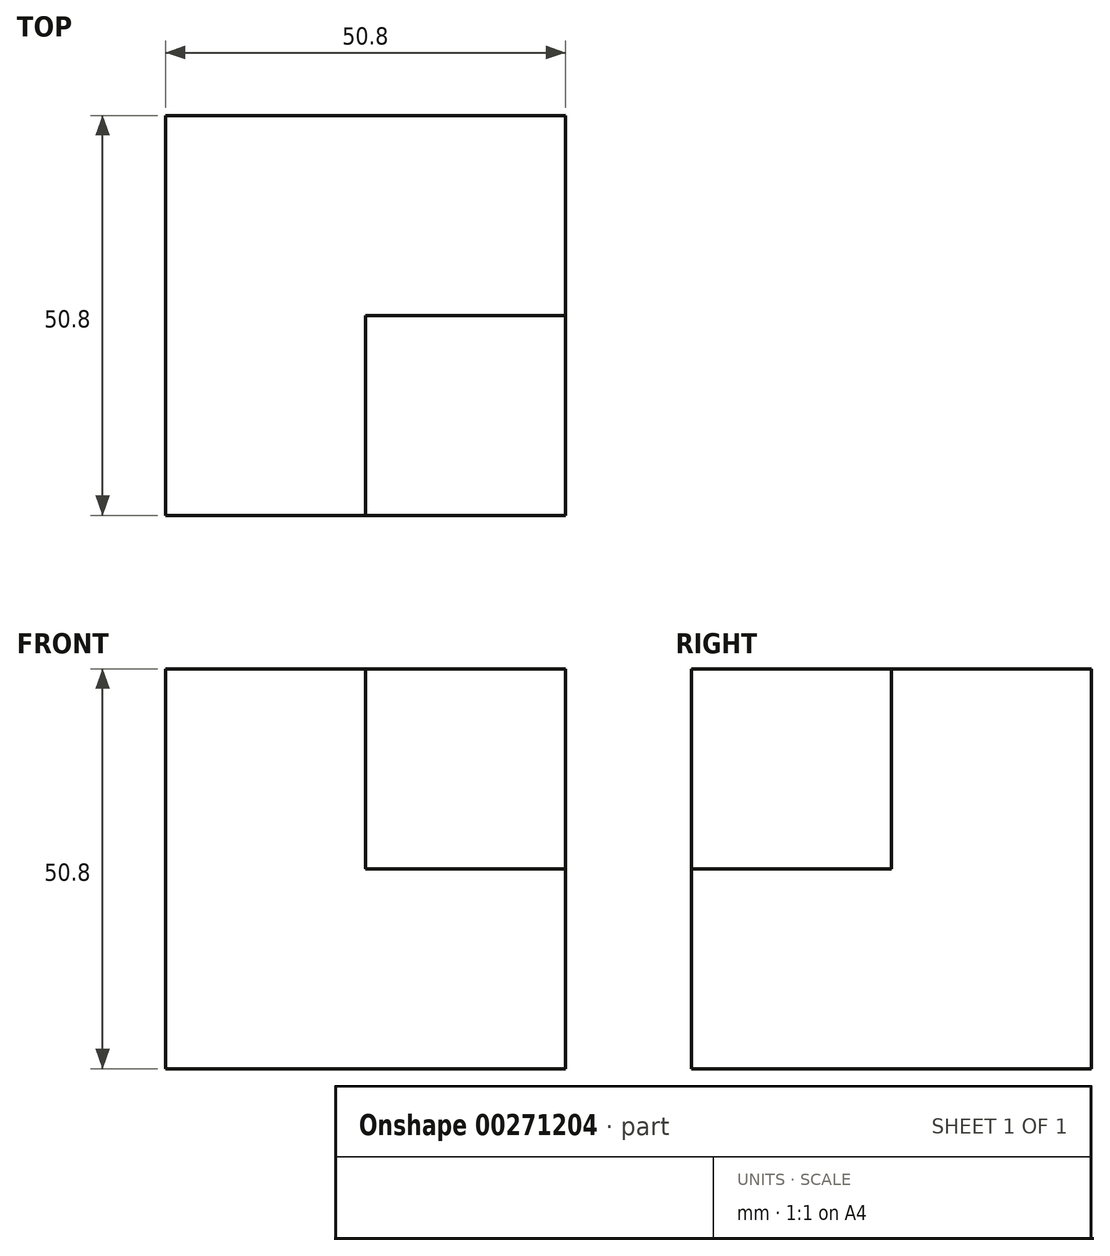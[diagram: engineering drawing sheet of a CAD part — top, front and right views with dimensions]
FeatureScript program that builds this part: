
annotation { "Feature Type Name" : "Feature", "Feature Type Description" : "" }
export const myFeature = defineFeature(function(context is Context, id is Id, definition is map)
    precondition{}
    {
        {
            var Q0;
            Q0=qCreatedBy(makeId("Front.planeOp"),FACE);
            var sketch = newSketch(context, id + "F0", { "sketchPlane" : qUnion([Q0])});
            skLineSegment(sketch, "E0.bottom", {"start": v(0, 0) * mm, "end": v(-50.8, 0) * mm});
            skLineSegment(sketch, "E0.top", {"start": v(0, 50.8) * mm, "end": v(-50.8, 50.8) * mm});
            skLineSegment(sketch, "E0.left", {"start": v(0, 0) * mm, "end": v(0, 50.8) * mm});
            skLineSegment(sketch, "E0.right", {"start": v(-50.8, 0) * mm, "end": v(-50.8, 50.8) * mm});
            skSolve(sketch);
        }
        {
            var Q0;
            Q0 = qSketchRegion(id + "F0", true);
            extrude(context, id + "F1", {"entities" : qUnion([Q0]), "depth" : 50.8 * mm});
        }
        {
            var Q0;
            Q0=makeQuery(id+"F1.opExtrude","CAP_FACE",FACE,{"disambiguationData":[OSD([sQuery(id+"F0.wireOp",EDGE,"E0.bottom"),sQuery(id+"F0.wireOp",EDGE,"E0.top"),sQuery(id+"F0.wireOp",EDGE,"E0.left"),sQuery(id+"F0.wireOp",EDGE,"E0.right")])],"isStart":false});
            var sketch = newSketch(context, id + "F2", { "sketchPlane" : qUnion([Q0])});
            skLineSegment(sketch, "E1", {"start": v(0, 50.8) * mm, "end": v(-25.4, 50.8) * mm});
            skLineSegment(sketch, "E2", {"start": v(-25.4, 50.8) * mm, "end": v(-25.4, 25.4) * mm});
            skLineSegment(sketch, "E3", {"start": v(-25.4, 25.4) * mm, "end": v(0, 25.4) * mm});
            skLineSegment(sketch, "E4", {"start": v(0, 25.4) * mm, "end": v(0, 50.8) * mm});
            skSolve(sketch);
        }
        {
            var Q0;
            Q0 = qSketchRegion(id + "F2", true);
            extrude(context, id + "F3", {"entities" : qUnion([Q0]), "operationType" : NewBodyOperationType.REMOVE, "oppositeDirection" : true, "depth" : 25.4 * mm});
        }
    });
